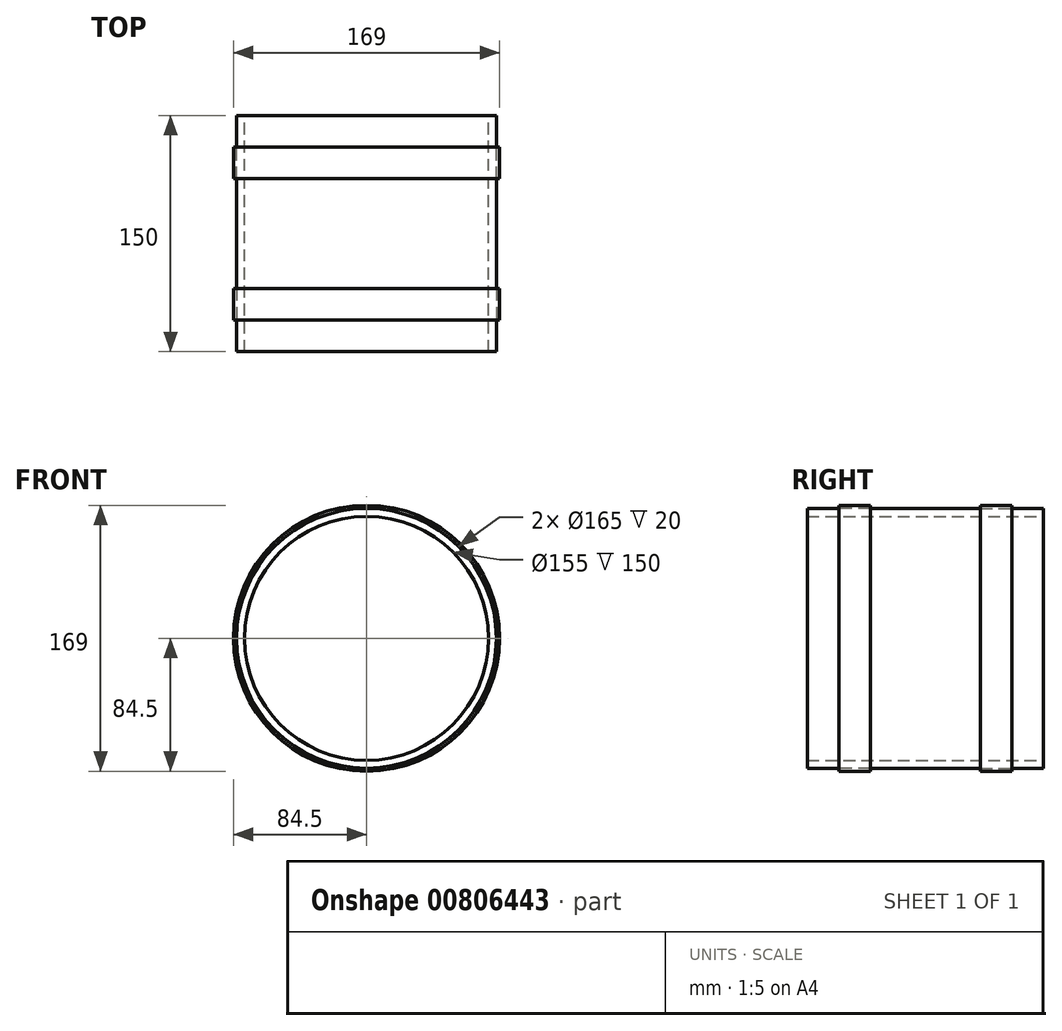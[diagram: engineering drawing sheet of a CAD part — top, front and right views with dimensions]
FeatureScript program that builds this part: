
annotation { "Feature Type Name" : "Feature", "Feature Type Description" : "" }
export const myFeature = defineFeature(function(context is Context, id is Id, definition is map)
    precondition{}
    {
        {
            var Q0;
            Q0=qCreatedBy(makeId("Front.planeOp"),FACE);
            var sketch = newSketch(context, id + "F0", { "sketchPlane" : qUnion([Q0])});
            skCircle(sketch, "E0", {"center": v(0, 0) * mm, "radius": 77.5 * mm});
            skCircle(sketch, "E1", {"center": v(0, 0) * mm, "radius": 82.5 * mm});
            skSolve(sketch);
        }
        {
            var Q0;
            Q0 = qSketchRegion(id + "F0", true);
            extrude(context, id + "F1", {"entities" : qUnion([Q0]), "depth" : 150 * mm, "offsetDistance" : 25 * mm});
        }
        {
            var Q0;
            Q0=makeQuery(id+"F1.opExtrude","CAP_FACE",FACE,{"disambiguationData":[OSD([sQuery(id+"F0.wireOp",EDGE,"E0"),sQuery(id+"F0.wireOp",EDGE,"E1")])],"isStart":false});
            var sketch = newSketch(context, id + "F2", { "sketchPlane" : qUnion([Q0])});
            skCircle(sketch, "E2", {"center": v(0, 0) * mm, "radius": 82.5 * mm});
            skCircle(sketch, "E3", {"center": v(0, 0) * mm, "radius": 84.5 * mm});
            skSolve(sketch);
        }
        {
            var Q0;
            Q0=makeQuery(id+"F2.imprint","IMPRINT",FACE,{"disambiguationData":[TD([[makeQuery(id+"F2.imprint","IMPRINT",EDGE,{"derivedFrom":sQuery(id+"F2.wireOp",EDGE,"E2")}),-1.0]])]});
            extrude(context, id + "F3", {"entities" : qUnion([Q0]), "oppositeDirection" : true, "depth" : 40 * mm, "offsetDistance" : 25 * mm});
        }
        {
            var Q0;
            Q0=makeQuery(id+"F3.opExtrude","CAP_FACE",FACE,{"disambiguationData":[OSD([sQuery(id+"F2.wireOp",EDGE,"E2"),sQuery(id+"F2.wireOp",EDGE,"E3")])],"isStart":true});
            extrude(context, id + "F4", {"entities" : qUnion([Q0]), "operationType" : NewBodyOperationType.REMOVE, "oppositeDirection" : true, "depth" : 20 * mm, "offsetDistance" : 25 * mm});
        }
        {
            var Q0;
            Q0=makeQuery(id+"F1.opExtrude","CAP_FACE",FACE,{"disambiguationData":[OSD([sQuery(id+"F0.wireOp",EDGE,"E0"),sQuery(id+"F0.wireOp",EDGE,"E1")])],"isStart":true});
            var sketch = newSketch(context, id + "F5", { "sketchPlane" : qUnion([Q0])});
            skCircle(sketch, "E4", {"center": v(0, 0) * mm, "radius": 82.5 * mm});
            skCircle(sketch, "E5", {"center": v(0, 0) * mm, "radius": 84.5 * mm});
            skSolve(sketch);
        }
        {
            var Q0;
            Q0=makeQuery(id+"F5.imprint","IMPRINT",FACE,{"disambiguationData":[TD([[makeQuery(id+"F5.imprint","IMPRINT",EDGE,{"derivedFrom":sQuery(id+"F5.wireOp",EDGE,"E4")}),1.0]])]});
            extrude(context, id + "F6", {"entities" : qUnion([Q0]), "oppositeDirection" : true, "depth" : 40 * mm, "offsetDistance" : 25 * mm});
        }
        {
            var Q0;
            Q0 = qSketchRegion(id + "F5", true);
            var Q1;
            Q1=makeQuery(id+"F6.opExtrude","CAP_FACE",FACE,{"disambiguationData":[OSD([sQuery(id+"F5.wireOp",EDGE,"E4"),sQuery(id+"F5.wireOp",EDGE,"E5")])],"isStart":true});
            extrude(context, id + "F7", {"entities" : qUnion([Q0, Q1]), "operationType" : NewBodyOperationType.REMOVE, "oppositeDirection" : true, "depth" : 20 * mm, "offsetDistance" : 25 * mm});
        }
    });
